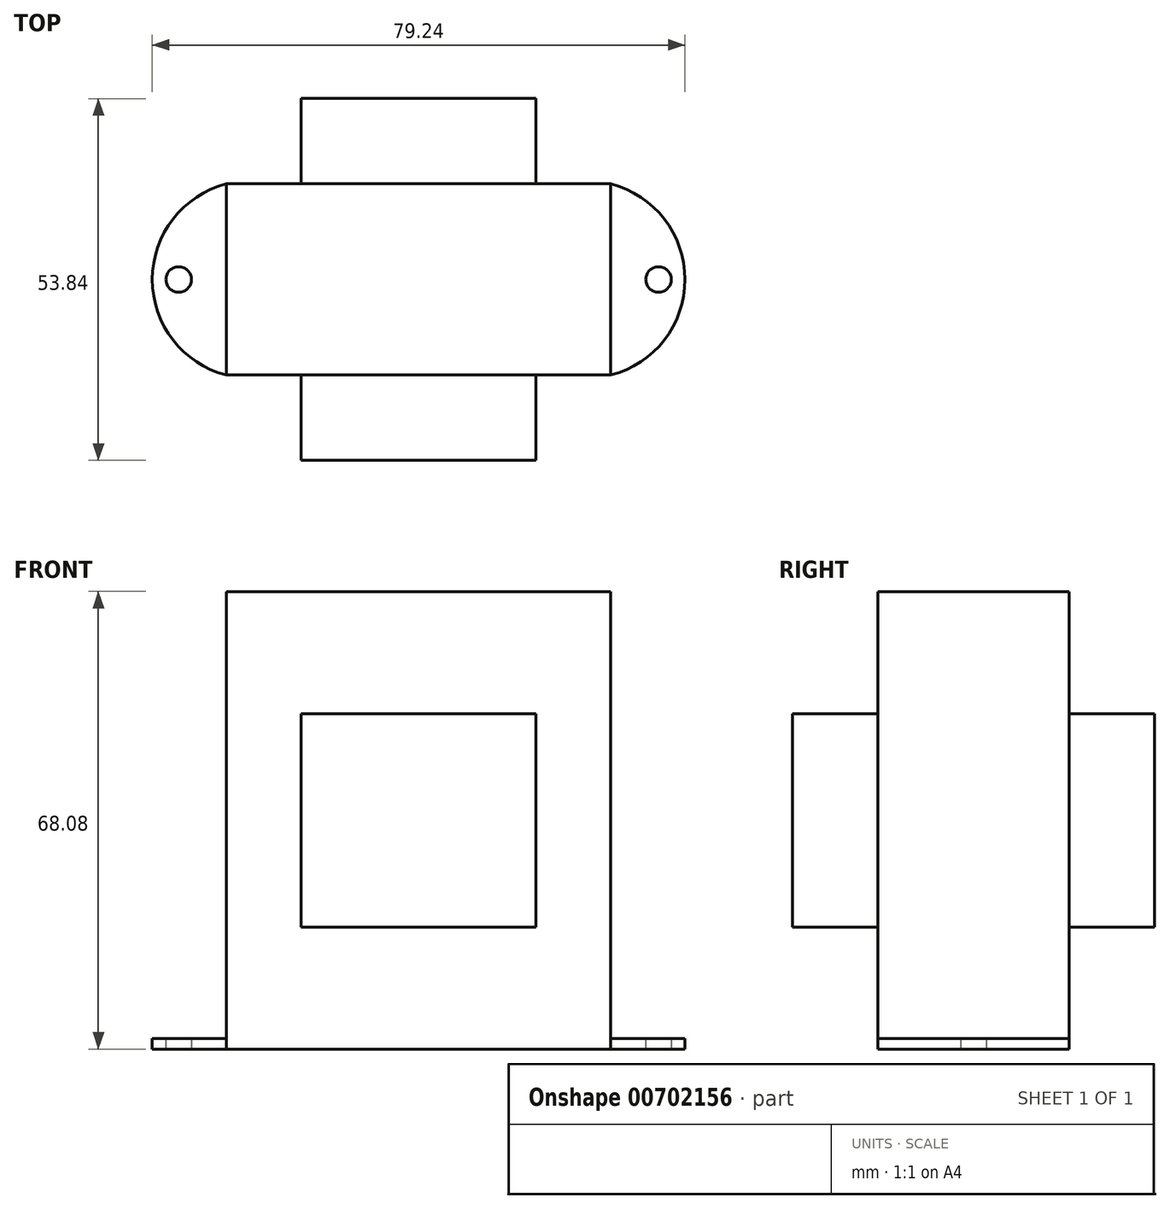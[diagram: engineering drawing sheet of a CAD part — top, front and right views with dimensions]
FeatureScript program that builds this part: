
annotation { "Feature Type Name" : "Feature", "Feature Type Description" : "" }
export const myFeature = defineFeature(function(context is Context, id is Id, definition is map)
    precondition{}
    {
        {
            var Q0;
            Q0=qCreatedBy(makeId("Front.planeOp"),FACE);
            var sketch = newSketch(context, id + "F0", { "sketchPlane" : qUnion([Q0])});
            skLineSegment(sketch, "E0.bottom", {"start": v(28.57, 34.04) * mm, "end": v(-28.58, 34.04) * mm});
            skLineSegment(sketch, "E0.top", {"start": v(28.58, -34.04) * mm, "end": v(-28.57, -34.04) * mm});
            skLineSegment(sketch, "E0.left", {"start": v(28.57, 34.04) * mm, "end": v(28.58, -34.04) * mm});
            skLineSegment(sketch, "E0.right", {"start": v(-28.58, 34.04) * mm, "end": v(-28.57, -34.04) * mm});
            skPoint(sketch, "E0.middle", {"position": v(0, 0) * mm});
            skSolve(sketch);
        }
        {
            var Q0;
            Q0 = qSketchRegion(id + "F0", true);
            extrude(context, id + "F1", {"entities" : qUnion([Q0]), "endBound" : BoundingType.SYMMETRIC, "depth" : 28.45 * mm, "offsetDistance" : 25.4 * mm});
        }
        {
            var Q0;
            Q0=qCreatedBy(makeId("Front.planeOp"),FACE);
            var sketch = newSketch(context, id + "F2", { "sketchPlane" : qUnion([Q0])});
            skLineSegment(sketch, "E1.bottom", {"start": v(17.46, 15.88) * mm, "end": v(-17.46, 15.88) * mm});
            skLineSegment(sketch, "E1.top", {"start": v(17.46, -15.88) * mm, "end": v(-17.46, -15.88) * mm});
            skLineSegment(sketch, "E1.left", {"start": v(17.46, 15.88) * mm, "end": v(17.46, -15.88) * mm});
            skLineSegment(sketch, "E1.right", {"start": v(-17.46, 15.88) * mm, "end": v(-17.46, -15.88) * mm});
            skPoint(sketch, "E1.middle", {"position": v(0, 0) * mm});
            skSolve(sketch);
        }
        {
            var Q0;
            Q0 = qSketchRegion(id + "F2", true);
            extrude(context, id + "F3", {"entities" : qUnion([Q0]), "operationType" : NewBodyOperationType.ADD, "endBound" : BoundingType.SYMMETRIC, "depth" : 53.85 * mm, "offsetDistance" : 25.4 * mm});
        }
        {
            var Q0;
            Q0=makeQuery(id+"F1.opExtrude","SWEPT_FACE",FACE,{"disambiguationData":[OSD([sQuery(id+"F0.wireOp",EDGE,"E0.top")])]});
            var sketch = newSketch(context, id + "F4", { "sketchPlane" : qUnion([Q0])});
            skArc(sketch, "E2", {"start": v(-28.58, 14.22) * mm, "mid": v(-39.62, 0) * mm, "end": v(-28.57, -14.22) * mm});
            skArc(sketch, "E3", {"start": v(28.58, -14.22) * mm, "mid": v(39.62, 0) * mm, "end": v(28.58, 14.22) * mm});
            skLineSegment(sketch, "E4", {"start": v(39.62, 0) * mm, "end": v(-39.62, 0) * mm, "construction": true});
            skSolve(sketch);
        }
        {
            var Q0;
            Q0 = qSketchRegion(id + "F4", true);
            var Q1;
            Q1=makeQuery(id+"F4.imprint","IMPRINT",FACE,{"disambiguationData":[TD([[makeQuery(id+"F4.imprint","IMPRINT",EDGE,{"derivedFrom":sQuery(id+"F4.wireOp",EDGE,"E2")}),1.0]])]});
            var Q2;
            Q2=makeQuery(id+"F4.imprint","IMPRINT",FACE,{"disambiguationData":[TD([[makeQuery(id+"F4.imprint","IMPRINT",EDGE,{"derivedFrom":sQuery(id+"F4.wireOp",EDGE,"E3")}),1.0]])]});
            extrude(context, id + "F5", {"entities" : qUnion([Q0, Q1, Q2]), "operationType" : NewBodyOperationType.ADD, "oppositeDirection" : true, "depth" : 1.59 * mm, "offsetDistance" : 25.4 * mm});
        }
        {
            var Q0;
            {var subQ0=sQuery(id+"F0.wireOp",EDGE,"E0.top");Q0=makeQuery(id+"F5.boolean.opBoolean","MERGE",FACE,{"derivedFrom":[makeQuery(id+"F1.opExtrude","SWEPT_FACE",FACE,{"disambiguationData":[OSD([subQ0])]}),makeQuery(id+"F5.opExtrude","CAP_FACE",FACE,{"disambiguationData":[OSD([subQ0,sQuery(id+"F0.wireOp",EDGE,"E0.right"),sQuery(id+"F4.wireOp",EDGE,"E2")])],"isStart":true}),makeQuery(id+"F5.opExtrude","CAP_FACE",FACE,{"disambiguationData":[OSD([subQ0,sQuery(id+"F0.wireOp",EDGE,"E0.left"),sQuery(id+"F4.wireOp",EDGE,"E3")])],"isStart":true})]});}
            var sketch = newSketch(context, id + "F6", { "sketchPlane" : qUnion([Q0])});
            skLineSegment(sketch, "E5", {"start": v(-35.69, 0) * mm, "end": v(35.69, 0) * mm});
            skSolve(sketch);
        }
        {
            var Q0;
            Q0=sQuery(id+"F6.wireOp",VERTEX,"E5.start");
            var Q1;
            Q1=sQuery(id+"F6.wireOp",VERTEX,"E5.end");
            var Q2;
            Q2=makeQuery(id+"F1.opExtrude","SWEPT_BODY",BODY,{"disambiguationData":[OSD([sQuery(id+"F0.wireOp",EDGE,"E0.bottom"),sQuery(id+"F0.wireOp",EDGE,"E0.top"),sQuery(id+"F0.wireOp",EDGE,"E0.left"),sQuery(id+"F0.wireOp",EDGE,"E0.right")])]});
            hole(context, id + "F7", {"style" : HoleStyle.SIMPLE, "endStyle" : HoleEndStyle.BLIND, "standardTappedOrClearance" : lookupTablePath({ "standard" : "ANSI", "fit" : "Normal (ASME)", "size" : "#6", "type" : "Clearance" }), "standardBlindInLast" : lookupTablePath({ "fit" : "Free", "standard" : "ANSI", "size" : "#6", "type" : "Clearance" }), "holeDiameter" : 3.8 * mm, "majorDiameter" : 6.35 * mm, "holeDepth" : 14.6 * mm, "isTappedThrough" : true, "tappedDepth" : 12.7 * mm, "tapClearance" : 3, "locations" : qUnion([Q0, Q1]), "scope" : qUnion([Q2])});
        }
    });
